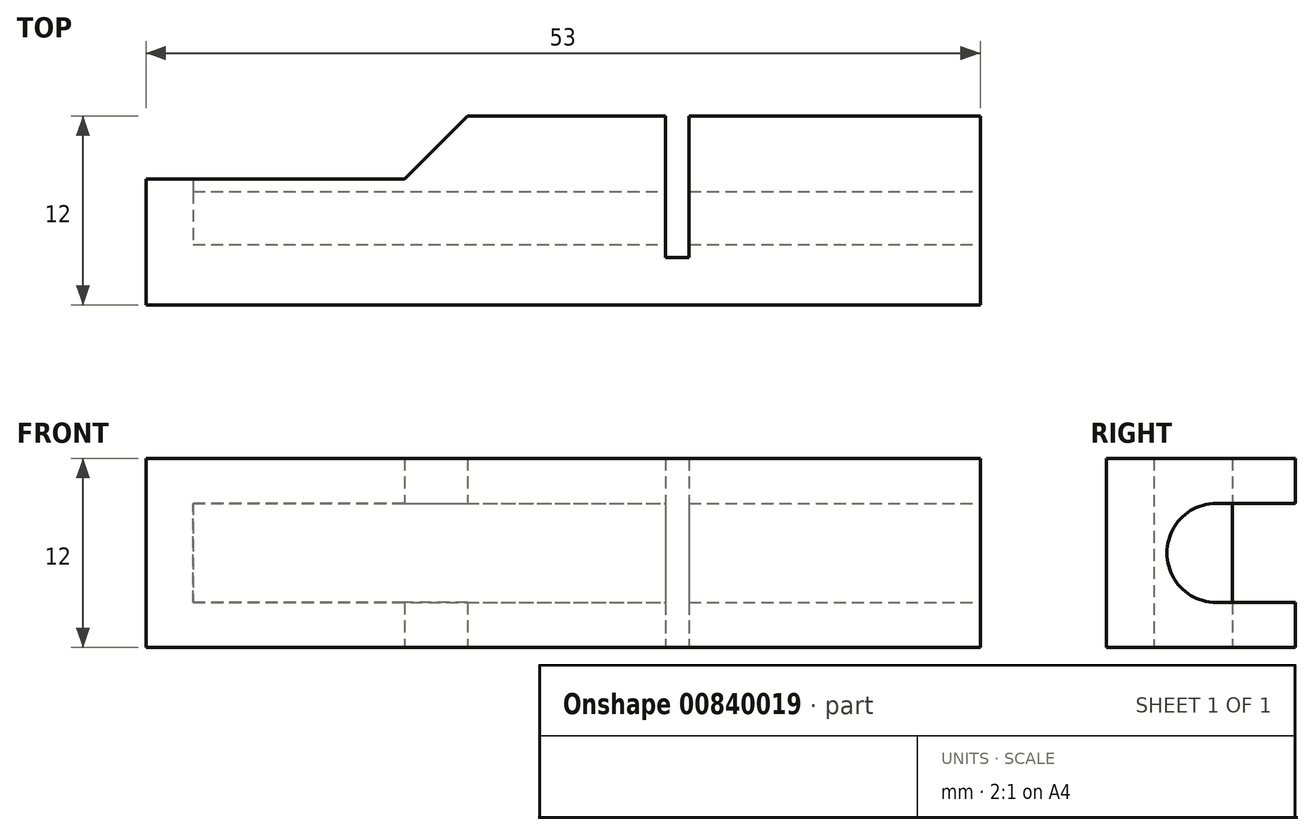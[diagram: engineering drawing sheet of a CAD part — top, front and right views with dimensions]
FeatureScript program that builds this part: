
annotation { "Feature Type Name" : "Feature", "Feature Type Description" : "" }
export const myFeature = defineFeature(function(context is Context, id is Id, definition is map)
    precondition{}
    {
        {
            var Q0;
            Q0=qCreatedBy(makeId("Top.planeOp"),FACE);
            var sketch = newSketch(context, id + "F0", { "sketchPlane" : qUnion([Q0])});
            skLineSegment(sketch, "E0.bottom", {"start": v(0, 0) * mm, "end": v(93, 0) * mm});
            skLineSegment(sketch, "E0.top", {"start": v(0, 10) * mm, "end": v(93, 10) * mm});
            skLineSegment(sketch, "E0.left", {"start": v(0, 0) * mm, "end": v(0, 10) * mm});
            skLineSegment(sketch, "E0.right", {"start": v(93, 0) * mm, "end": v(93, 10) * mm});
            skSolve(sketch);
        }
        {
            var Q0;
            Q0 = qSketchRegion(id + "F0", true);
            extrude(context, id + "F1", {"entities" : qUnion([Q0]), "depth" : 12 * mm, "offsetDistance" : 25 * mm});
        }
        {
            var Q0;
            Q0=makeQuery(id+"F1.opExtrude","SWEPT_FACE",FACE,{"disambiguationData":[OSD([sQuery(id+"F0.wireOp",EDGE,"E0.right")])]});
            var sketch = newSketch(context, id + "F2", { "sketchPlane" : qUnion([Q0])});
            skCircle(sketch, "E1", {"center": v(5, 6) * mm, "radius": 3.15 * mm});
            skPoint(sketch, "E1.centerSnap0", {"position": v(5, 12) * mm});
            skPoint(sketch, "E1.centerSnap1", {"position": v(10, 6) * mm});
            skLineSegment(sketch, "E2.bottom", {"start": v(10, 6) * mm, "end": v(4.8, 6) * mm});
            skLineSegment(sketch, "E2.top", {"start": v(10, 2.86) * mm, "end": v(4.8, 2.86) * mm});
            skLineSegment(sketch, "E2.left", {"start": v(10, 6) * mm, "end": v(10, 2.86) * mm});
            skLineSegment(sketch, "E2.right", {"start": v(4.8, 6) * mm, "end": v(4.8, 2.86) * mm});
            skLineSegment(sketch, "E3.MirrorCS", {"start": v(10, 6) * mm, "end": v(10, 9.14) * mm});
            skLineSegment(sketch, "E4.MirrorCS", {"start": v(10, 9.14) * mm, "end": v(4.8, 9.14) * mm});
            skLineSegment(sketch, "E5.MirrorCS", {"start": v(4.8, 6) * mm, "end": v(4.8, 9.14) * mm});
            skSolve(sketch);
        }
        {
            var Q0;
            Q0 = qSketchRegion(id + "F2", true);
            extrude(context, id + "F3", {"entities" : qUnion([Q0]), "operationType" : NewBodyOperationType.REMOVE, "oppositeDirection" : true, "depth" : 90 * mm, "offsetDistance" : 25 * mm});
        }
        {
            var Q0;
            Q0=makeQuery(id+"F3.boolean.opBoolean","COPY",FACE,{"derivedFrom":makeQuery(id+"F3.opExtrude","CAP_FACE",FACE,{"disambiguationData":[OSD([sQuery(id+"F2.wireOp",EDGE,"E1"),sQuery(id+"F2.wireOp",EDGE,"E2.top"),sQuery(id+"F2.wireOp",EDGE,"E2.left"),sQuery(id+"F2.wireOp",EDGE,"E3.MirrorCS"),sQuery(id+"F2.wireOp",EDGE,"E4.MirrorCS")])],"isStart":false})});
            cPlane(context, id + "F4", {"entities" : qUnion([Q0]), "cplaneType" : CPlaneType.OFFSET, "offset" : 30 * mm, "width" : 150 * mm, "height" : 150 * mm});
        }
        {
            var Q0;
            Q0=qCreatedBy(id+"F4.planeOp",FACE);
            var sketch = newSketch(context, id + "F5", { "sketchPlane" : qUnion([Q0])});
            skPoint(sketch, "E6.0", {"position": v(10, 12) * mm});
            skPoint(sketch, "E7.0", {"position": v(10, 0) * mm});
            skLineSegment(sketch, "E8.bottom", {"start": v(10, 12) * mm, "end": v(1.03, 12) * mm});
            skLineSegment(sketch, "E8.top", {"start": v(10, 0) * mm, "end": v(1.03, 0) * mm});
            skLineSegment(sketch, "E8.left", {"start": v(10, 12) * mm, "end": v(10, 0) * mm});
            skLineSegment(sketch, "E8.right", {"start": v(1.03, 12) * mm, "end": v(1.03, 0) * mm});
            skSolve(sketch);
        }
        {
            var Q0;
            Q0 = qSketchRegion(id + "F5", true);
            extrude(context, id + "F6", {"entities" : qUnion([Q0]), "operationType" : NewBodyOperationType.REMOVE, "depth" : 1.5 * mm, "offsetDistance" : 25 * mm});
        }
        {
            var Q0;
            Q0=makeQuery(id+"F1.opExtrude","SWEPT_FACE",FACE,{"disambiguationData":[OSD([sQuery(id+"F0.wireOp",EDGE,"E0.bottom")])]});
            extrude(context, id + "F7", {"entities" : qUnion([Q0]), "operationType" : NewBodyOperationType.ADD, "depth" : 2 * mm, "offsetDistance" : 25 * mm});
        }
        {
            var Q0;
            {var subQ0=sQuery(id+"F0.wireOp",EDGE,"E0.right");Q0=makeQuery(id+"F7.boolean.opBoolean","MERGE",FACE,{"derivedFrom":[makeQuery(id+"F1.opExtrude","SWEPT_FACE",FACE,{"disambiguationData":[OSD([subQ0])]}),makeQuery(id+"F7.opExtrude","SWEPT_FACE",FACE,{"disambiguationData":[OSD([sQuery(id+"F0.wireOp",EDGE,"E0.bottom"),subQ0])]})]});}
            extrude(context, id + "F8", {"entities" : qUnion([Q0]), "operationType" : NewBodyOperationType.REMOVE, "oppositeDirection" : true, "depth" : 40 * mm, "offsetDistance" : 25 * mm});
        }
        {
            var Q0;
            {var subQ0=sQuery(id+"F2.wireOp",EDGE,"E4.MirrorCS");var subQ1=sQuery(id+"F2.wireOp",EDGE,"E2.top");var subQ2=sQuery(id+"F0.wireOp",EDGE,"E0.left");var subQ3=sQuery(id+"F0.wireOp",EDGE,"E0.right");var subQ4=sQuery(id+"F0.wireOp",EDGE,"E0.top");var subQ5=sQuery(id+"F0.wireOp",EDGE,"E0.bottom");Q0=makeQuery(id+"F6.boolean.opBoolean","SPLIT",FACE,{"disambiguationData":[TD([makeQuery(id+"F1.opExtrude","CAP_FACE",FACE,{"disambiguationData":[OSD([subQ5,subQ4,subQ2,subQ3])],"isStart":true}),makeQuery(id+"F1.opExtrude","CAP_FACE",FACE,{"disambiguationData":[OSD([subQ5,subQ4,subQ2,subQ3])],"isStart":false}),makeQuery(id+"F1.opExtrude","SWEPT_FACE",FACE,{"disambiguationData":[OSD([subQ2])]}),makeQuery(id+"F3.boolean.opBoolean","COPY",FACE,{"derivedFrom":makeQuery(id+"F3.opExtrude","CAP_FACE",FACE,{"disambiguationData":[OSD([sQuery(id+"F2.wireOp",EDGE,"E1"),subQ1,sQuery(id+"F2.wireOp",EDGE,"E2.left"),sQuery(id+"F2.wireOp",EDGE,"E3.MirrorCS"),subQ0])],"isStart":false})}),makeQuery(id+"F3.boolean.opBoolean","COPY",FACE,{"derivedFrom":makeQuery(id+"F3.opExtrude","SWEPT_FACE",FACE,{"disambiguationData":[OSD([subQ1])]})}),makeQuery(id+"F3.boolean.opBoolean","COPY",FACE,{"derivedFrom":makeQuery(id+"F3.opExtrude","SWEPT_FACE",FACE,{"disambiguationData":[OSD([subQ0])]})}),makeQuery(id+"F6.opExtrude","CAP_FACE",FACE,{"disambiguationData":[OSD([sQuery(id+"F5.wireOp",EDGE,"E8.bottom"),sQuery(id+"F5.wireOp",EDGE,"E8.top"),sQuery(id+"F5.wireOp",EDGE,"E8.left"),sQuery(id+"F5.wireOp",EDGE,"E8.right")])],"isStart":true})])],"derivedFrom":makeQuery(id+"F1.opExtrude","SWEPT_FACE",FACE,{"disambiguationData":[OSD([subQ4])]})});}
            var sketch = newSketch(context, id + "F9", { "sketchPlane" : qUnion([Q0])});
            skLineSegment(sketch, "E9.bottom", {"start": v(0, 12) * mm, "end": v(-20.42, 12) * mm});
            skLineSegment(sketch, "E9.top", {"start": v(0, 0) * mm, "end": v(-20.42, 0) * mm});
            skLineSegment(sketch, "E9.left", {"start": v(0, 12) * mm, "end": v(0, 0) * mm});
            skLineSegment(sketch, "E9.right", {"start": v(-20.42, 12) * mm, "end": v(-20.42, 0) * mm});
            skSolve(sketch);
        }
        {
            var Q0;
            Q0 = qSketchRegion(id + "F9", true);
            extrude(context, id + "F10", {"entities" : qUnion([Q0]), "operationType" : NewBodyOperationType.REMOVE, "oppositeDirection" : true, "depth" : 4 * mm, "offsetDistance" : 25 * mm});
        }
        {
            var Q0;
            {var subQ0=sQuery(id+"F9.wireOp",EDGE,"E9.right");Q0=makeQuery(id+"F10.boolean.opBoolean","COPY",EDGE,{"disambiguationData":[TD([makeQuery(id+"F3.boolean.opBoolean","COPY",FACE,{"derivedFrom":makeQuery(id+"F3.opExtrude","SWEPT_FACE",FACE,{"disambiguationData":[OSD([sQuery(id+"F2.wireOp",EDGE,"E2.top")])]})})])],"derivedFrom":makeQuery(id+"F10.opExtrude","CAP_EDGE",EDGE,{"disambiguationData":[OSD([subQ0])],"isStart":false})});}
            var Q1;
            {var subQ0=sQuery(id+"F9.wireOp",EDGE,"E9.right");Q1=makeQuery(id+"F10.boolean.opBoolean","COPY",EDGE,{"disambiguationData":[TD([makeQuery(id+"F3.boolean.opBoolean","COPY",FACE,{"derivedFrom":makeQuery(id+"F3.opExtrude","SWEPT_FACE",FACE,{"disambiguationData":[OSD([sQuery(id+"F2.wireOp",EDGE,"E4.MirrorCS")])]})})])],"derivedFrom":makeQuery(id+"F10.opExtrude","CAP_EDGE",EDGE,{"disambiguationData":[OSD([subQ0])],"isStart":false})});}
            chamfer(context, id + "F11", {"entities" : qUnion([Q0, Q1]), "width" : 4 * mm, "tangentPropagation" : true});
        }
    });
